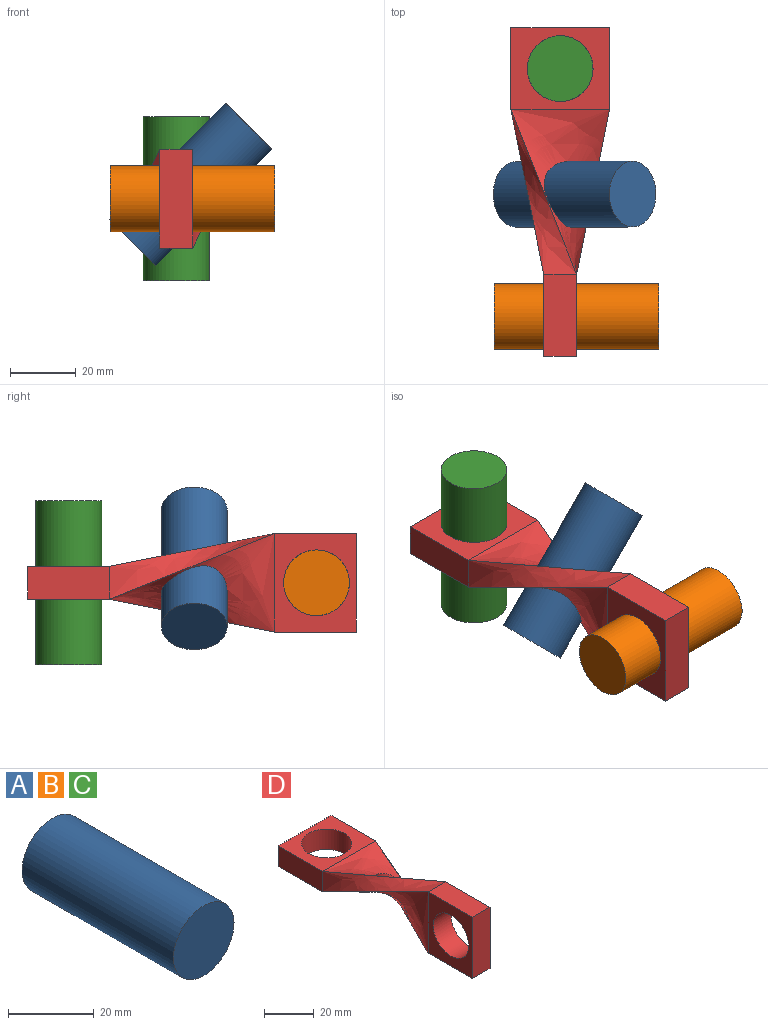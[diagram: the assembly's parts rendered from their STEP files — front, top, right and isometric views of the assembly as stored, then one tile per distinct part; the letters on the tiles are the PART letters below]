
ASSEMBLY  parts=4 mates=3
PART A: 3 faces, bbox 20x50x20 mm
  f0: cylinder r=10mm len=50mm, axis (0,1,0), area 3141.6mm2, adj f1,f2
  f1: plane 20x20mm, normal (0,-1,0), area 314.2mm2, adj f0
  f2: plane 20x20mm, normal (0,1,0), area 314.2mm2, adj f0
PART B: same geometry as A
PART C: same geometry as A
PART D: 17 faces, bbox 30x100x30 mm
  f0: bspline ~50x30mm, area 920.7mm2, adj f2,f3,f5,f9,f16
  f1: bspline ~50x30mm, area 920.6mm2, adj f2,f3,f7,f11,f16
  f2: bspline ~50x20mm, area 415.1mm2, adj f0,f1,f4,f10
  f3: bspline ~50x20mm, area 415.1mm2, adj f0,f1,f6,f12
  f4: plane 25x10mm, normal (0,0,-1), area 250mm2, adj f2,f5,f7,f8
  f5: plane 30x25mm, normal (1,0,0), area 435.8mm2, adj f0,f4,f6,f8,f14
  f6: plane 25x10mm, normal (0,0,1), area 250mm2, adj f3,f5,f7,f8
  f7: plane 30x25mm, normal (-1,0,0), area 435.8mm2, adj f1,f4,f6,f8,f14
  f8: plane 30x10mm, normal (0,-1,0), area 300mm2, adj f4,f5,f6,f7
  f9: plane 30x25mm, normal (0,0,1), area 435.8mm2, adj f0,f10,f12,f13,f15
  f10: plane 25x10mm, normal (1,0,0), area 250mm2, adj f2,f9,f11,f13
  f11: plane 30x25mm, normal (0,0,-1), area 435.8mm2, adj f1,f10,f12,f13,f15
  f12: plane 25x10mm, normal (-1,0,0), area 250mm2, adj f3,f9,f11,f13
  f13: plane 30x10mm, normal (0,1,0), area 300mm2, adj f9,f10,f11,f12
  f14: cylinder r=10mm len=20mm, axis (-1,0,0), area 628.3mm2, adj f5,f7
  f15: cylinder r=10mm len=20mm, axis (0,0,1), area 628.3mm2, adj f9,f11
  f16: cylinder r=10mm len=22.75mm, axis (-0.71,0,-0.71), area 480.3mm2, adj f0,f1
PLACE A rot(axis=(-0.86,0.36,0.36),98.4deg) t=(-15.08,6.49,-0.97)mm
PLACE B rot(axis=(0.58,-0.58,0.58),120deg) t=(-21.79,-30.71,12.32)mm
PLACE C rot(axis=(1,0,0),90deg) t=(-1.79,44.68,37.32)mm
PLACE D t=(-1.79,-17.82,12.32)mm
MATE slider B.f0 <-> D.f14  axis (-1,0,0) through (3.21,-30.71,12.32)mm
MATE slider A.f0 <-> D.f16  axis (-0.71,0,-0.71) through (2.6,6.49,16.7)mm
MATE slider C.f0 <-> D.f15  axis (0,0,1) through (-1.79,44.68,12.32)mm
